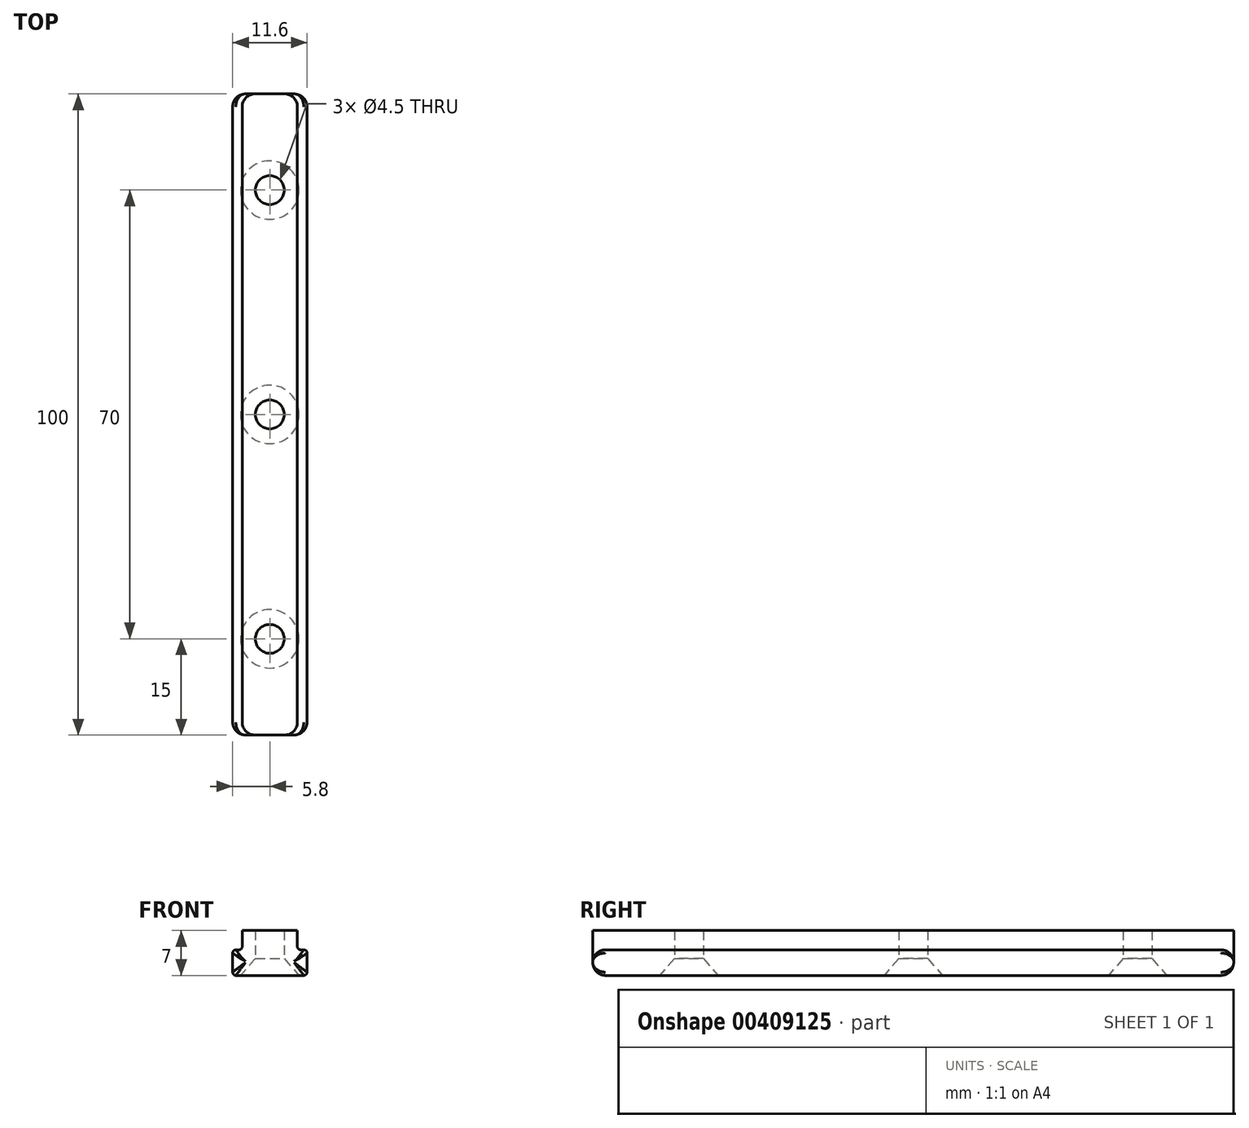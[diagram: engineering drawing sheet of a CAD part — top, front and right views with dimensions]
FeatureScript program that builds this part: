
annotation { "Feature Type Name" : "Feature", "Feature Type Description" : "" }
export const myFeature = defineFeature(function(context is Context, id is Id, definition is map)
    precondition{}
    {
        {
            var Q0;
            Q0=qCreatedBy(makeId("Front.planeOp"),FACE);
            var sketch = newSketch(context, id + "F0", { "sketchPlane" : qUnion([Q0])});
            skLineSegment(sketch, "E0", {"start": v(0, 0) * mm, "end": v(5.8, 0) * mm});
            skLineSegment(sketch, "E1", {"start": v(5.8, 0) * mm, "end": v(5.8, 4) * mm});
            skLineSegment(sketch, "E2", {"start": v(5.8, 4) * mm, "end": v(4.3, 4) * mm});
            skLineSegment(sketch, "E3", {"start": v(4.3, 4) * mm, "end": v(4.3, 7) * mm});
            skLineSegment(sketch, "E4", {"start": v(4.3, 7) * mm, "end": v(0, 7) * mm});
            skLineSegment(sketch, "E5", {"start": v(0, 0) * mm, "end": v(-5.8, 0) * mm});
            skLineSegment(sketch, "E6", {"start": v(-5.8, 0) * mm, "end": v(-5.8, 4) * mm});
            skLineSegment(sketch, "E7", {"start": v(-5.8, 4) * mm, "end": v(-4.3, 4) * mm});
            skLineSegment(sketch, "E8", {"start": v(-4.3, 4) * mm, "end": v(-4.3, 7) * mm});
            skLineSegment(sketch, "E9", {"start": v(-4.3, 7) * mm, "end": v(0, 7) * mm});
            skSolve(sketch);
        }
        {
            var Q0;
            Q0=makeQuery(id+"F0.imprint","IMPRINT",FACE,{"disambiguationData":[TD([[makeQuery(id+"F0.imprint","IMPRINT",EDGE,{"derivedFrom":sQuery(id+"F0.wireOp",EDGE,"E0")}),1.0]])]});
            extrude(context, id + "F1", {"entities" : qUnion([Q0]), "oppositeDirection" : true, "depth" : 100 * mm, "symmetric" : true});
        }
        {
            var Q0;
            Q0=makeQuery(id+"F1.opExtrude","SWEPT_FACE",FACE,{"disambiguationData":[OSD([sQuery(id+"F0.wireOp",EDGE,"E0"),sQuery(id+"F0.wireOp",EDGE,"E5")])]});
            var sketch = newSketch(context, id + "F2", { "sketchPlane" : qUnion([Q0])});
            skLineSegment(sketch, "E10", {"start": v(0, 54.75) * mm, "end": v(0, -56.35) * mm, "construction": true});
            skLineSegment(sketch, "E11", {"start": v(-11.08, 35) * mm, "end": v(14.13, 35) * mm, "construction": true});
            skLineSegment(sketch, "E12", {"start": v(-13, -35) * mm, "end": v(14.61, -35) * mm, "construction": true});
            skPoint(sketch, "E13", {"position": v(0, 35) * mm});
            skPoint(sketch, "E14", {"position": v(0, -35) * mm});
            skPoint(sketch, "E15", {"position": v(0, 0) * mm});
            skSolve(sketch);
        }
        {
            var Q0;
            Q0=sQuery(id+"F2.wireOp",VERTEX,"E13");
            var Q1;
            Q1=sQuery(id+"F2.wireOp",VERTEX,"E15");
            var Q2;
            Q2=sQuery(id+"F2.wireOp",VERTEX,"E14");
            var Q3;
            Q3=makeQuery(id+"F1.opExtrude","SWEPT_BODY",BODY,{"disambiguationData":[OSD([sQuery(id+"F0.wireOp",EDGE,"E0"),sQuery(id+"F0.wireOp",EDGE,"E1"),sQuery(id+"F0.wireOp",EDGE,"E2"),sQuery(id+"F0.wireOp",EDGE,"E3"),sQuery(id+"F0.wireOp",EDGE,"E4"),sQuery(id+"F0.wireOp",EDGE,"E5"),sQuery(id+"F0.wireOp",EDGE,"E6"),sQuery(id+"F0.wireOp",EDGE,"E7"),sQuery(id+"F0.wireOp",EDGE,"E8"),sQuery(id+"F0.wireOp",EDGE,"E9")])]});
            hole(context, id + "F3", {"style" : HoleStyle.C_SINK, "endStyle" : HoleEndStyle.THROUGH, "standardTappedOrClearance" : lookupTablePath({ "standard" : "ANSI", "fit" : "Normal (ASME)", "size" : "#8", "type" : "Clearance" }), "standardBlindInLast" : lookupTablePath({ "fit" : "Free", "standard" : "ANSI", "size" : "#8", "type" : "Clearance" }), "holeDiameter" : 4.5 * mm, "cSinkDiameter" : 9.12 * mm, "cSinkAngle" : 82 * degree, "isTappedThrough" : true, "tappedDepth" : 12 * mm, "tapClearance" : 3, "locations" : qUnion([Q0, Q1, Q2]), "scope" : qUnion([Q3])});
        }
        {
            var Q0;
            Q0=makeQuery(id+"F1.opExtrude","SWEPT_EDGE",EDGE,{"disambiguationData":[OSD([sQuery(id+"F0.wireOp",EDGE,"E2"),sQuery(id+"F0.wireOp",EDGE,"E3")])]});
            var Q1;
            Q1=makeQuery(id+"F1.opExtrude","SWEPT_EDGE",EDGE,{"disambiguationData":[OSD([sQuery(id+"F0.wireOp",EDGE,"E1"),sQuery(id+"F0.wireOp",EDGE,"E2")])]});
            var Q2;
            Q2=makeQuery(id+"F1.opExtrude","SWEPT_EDGE",EDGE,{"disambiguationData":[OSD([sQuery(id+"F0.wireOp",EDGE,"E0"),sQuery(id+"F0.wireOp",EDGE,"E1")])]});
            var Q3;
            Q3=makeQuery(id+"F1.opExtrude","SWEPT_EDGE",EDGE,{"disambiguationData":[OSD([sQuery(id+"F0.wireOp",EDGE,"E5"),sQuery(id+"F0.wireOp",EDGE,"E6")])]});
            var Q4;
            Q4=makeQuery(id+"F1.opExtrude","SWEPT_EDGE",EDGE,{"disambiguationData":[OSD([sQuery(id+"F0.wireOp",EDGE,"E6"),sQuery(id+"F0.wireOp",EDGE,"E7")])]});
            var Q5;
            Q5=makeQuery(id+"F1.opExtrude","SWEPT_EDGE",EDGE,{"disambiguationData":[OSD([sQuery(id+"F0.wireOp",EDGE,"E7"),sQuery(id+"F0.wireOp",EDGE,"E8")])]});
            fillet(context, id + "F4", {"entities" : qUnion([Q0, Q1, Q2, Q3, Q4, Q5]), "radius" : 0.5 * mm, "tangentPropagation" : true, "allowEdgeOverflow" : false});
        }
        {
            var Q0;
            Q0=makeQuery(id+"F1.opExtrude","CAP_EDGE",EDGE,{"disambiguationData":[OSD([sQuery(id+"F0.wireOp",EDGE,"E6")])],"isStart":true});
            var Q1;
            Q1=makeQuery(id+"F1.opExtrude","CAP_EDGE",EDGE,{"disambiguationData":[OSD([sQuery(id+"F0.wireOp",EDGE,"E0"),sQuery(id+"F0.wireOp",EDGE,"E5")])],"isStart":true});
            var Q2;
            Q2=makeQuery(id+"F1.opExtrude","CAP_EDGE",EDGE,{"disambiguationData":[OSD([sQuery(id+"F0.wireOp",EDGE,"E1")])],"isStart":true});
            var Q3;
            Q3=makeQuery(id+"F1.opExtrude","CAP_EDGE",EDGE,{"disambiguationData":[OSD([sQuery(id+"F0.wireOp",EDGE,"E0"),sQuery(id+"F0.wireOp",EDGE,"E5")])],"isStart":false});
            var Q4;
            Q4=makeQuery(id+"F1.opExtrude","CAP_EDGE",EDGE,{"disambiguationData":[OSD([sQuery(id+"F0.wireOp",EDGE,"E1")])],"isStart":false});
            fillet(context, id + "F5", {"entities" : qUnion([Q0, Q1, Q2, Q3, Q4]), "radius" : 2 * mm, "tangentPropagation" : true, "allowEdgeOverflow" : false});
        }
    });
